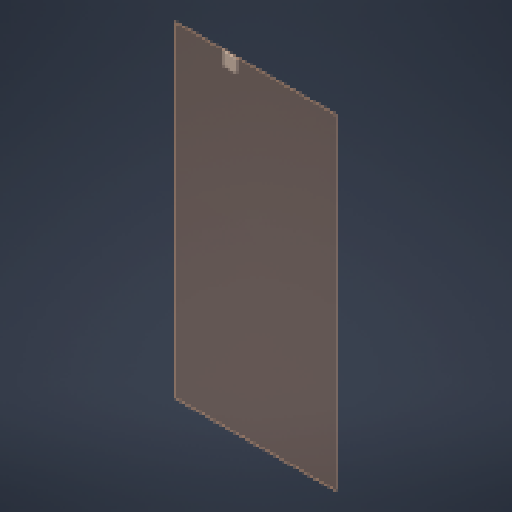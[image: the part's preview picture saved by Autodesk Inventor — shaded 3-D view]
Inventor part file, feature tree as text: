
AUTODESK INVENTOR PART (.ipt)
format: ipt  version: 2024 (Build 280153000, 153)  size: 127,488 bytes
history: native  units: mm
features: other x5, plane x1, extrude x1, sketch x1
ambient origin geometry x8: Origin, YZ Plane, XZ Plane, XY Plane, X Axis, Y Axis, Z Axis, Center Point
bodies: Body1 (feature_tree)
feature tree (8):
  other  "Sólido1"
  plane  "Plano de trabajo1"
  extrude  "Extrusión1"  Depth=30.0mm
  sketch  "Boceto1"  dims[d0=120.0mm d1=30.0mm d2=30.0mm d3=30.0mm d4=30.0mm d5=2.0mm d6=0.0mm]
  other  "<userpath>\Downloads\Piezas CMR\Marco_APM_001\Marco_apm_001-2.iam"
  other  "Marco_apm_001-2.iam"
  other  "Marco_Conveyor_Aereo:1"
  other  "Marco:1"
